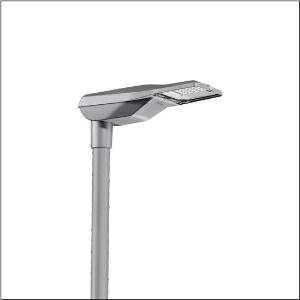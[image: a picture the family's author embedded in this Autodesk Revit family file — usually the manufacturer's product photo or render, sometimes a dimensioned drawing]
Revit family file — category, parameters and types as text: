
# Revit family: streetlight_sl_21_iq_micro___stw1_0a_5xe1e31g08cb_d673
name_source: partatom
category: Lighting Fixtures
units: mm (PartAtom-declared; Revit-internal decimal feet)

## family parameters
Cut with Voids When Loaded = No
Host = Face
Light Source = No
Part Type = Normal
Room Calculation Point = No
Round Connector Dimension = Use Diameter
Shared = No

## types (1)
- --- (1 x LED, 2870 lm, 19.4 W, 3000K)
    Apparent Load = 19 VA
    CIE Flux Codes = 38 75 98 100 100
    Color Rendering = 70
    Color Temperature = 3000K
    Default Elevation = 1800 mm
    Description = Streetlight SL 21 iQ micro, mast luminaire, primary light control with lens, of PMMA, primary optical cover: cover, of toughened safety glass, transparent, light distribution: STW1.0a, light emission: direct distribution, primary light characteristic: asymmetric, installation type: post-top, side-entry, LED, High Power LED, rated luminous flux: 2.870lm, luminous efficacy: 148lm/W, light colour: 730, colour temperature: 3000K, control: Street-Remote, Auto-Match, Temp-Guard, Lumen-Switch, Night-Set, Smart-Wire, Light-Fading, Desk-Remote (wireless, voltage-free reading and setting of iQ features in the workshop via application-optimized NFC function/RFID function), optimised constant luminous flux control (CLO 2.0), presetting dimming linear, mains connection: 220..240V, AC, 50/60Hz, start of lifetime: 19W, end of service life: 20W, reduction: 10W, luminaire housing, of diecast aluminium, powder-coated, Siteco® metallic grey (DB 702S), corrosivity category C5 mid according to DIN EN ISO 12944, please order mast flange separately, inclination adjustable: 0°, 5°, 10°, 15°, sealing non-destructively replaceable, multi-level sealing system, length: 528mm, width: 235mm, height: 110mm, mast flange for spigot size: 42mm (side-entry): 5XC10008XM4, 60/48mm (side-entry/post-top): 5XC10108XM2, 76/60mm (side-entry/post-top): 5XC10108XM1, protection rating (complete): IP66, insulation class (complete): insulation class II (safety insulation), certification: CE, ENEC, ENEC+, VDE, impact resistance: IK09, permissible operating ambient temperature for outdoor applications: -40..+50°C, standard-compliant lighting for roads and squares, packaging unit: 1 piece

Light Distribution: STW1.0a
    Height = 110 mm
    Lamp = 1 x LED
    Lamp Light Flux = 2870 lm
    Lamp Power = 19.4 W
    Lamp count = 1
    Length = 528 mm
    Luminous efficacy = 148 lm/W
    Manufacturer = Siteco
    ModVariant = No
    Model = 5XE1E31G08CB
    Number of Poles = 1
    OnlyDefault = Yes
    Power Factor = 1
    Product Name = Streetlight SL 21 iQ micro | STW1.0a
    Product group = mast luminaire | pylon top
    ProductGroupID = 6100
    Protection Class = Protection class II
    Protection Degree = IP 66
    RLX_Detail_Level = 1
    RLX_Emergency_Light_Flux = 0 lm
    RLX_Emergency_Type = 0
    RLX_Emergency_Type_DB = No
    RlxData = <blob elided: 98369 chars, md5=44ebd469>
    Socket = socket
    Standby Power = 0 W
    System Light Flux = 2870 lm
    System Power = 19 W
    Type Comments = factory setting: luminous flux: 100 % | dim-lin: 254 | 387 mA
    Type Image = l_1006881.jpg
    URL = http://relux.com
    VarID = @adj_070185
    Voltage = 0 V
    Weight = 0.00 kg
    Width = 235 mm

## geometry (parser evidence)
native form markers: Blend x4, Sweep x8
no freeform markers — native parametric forms only
